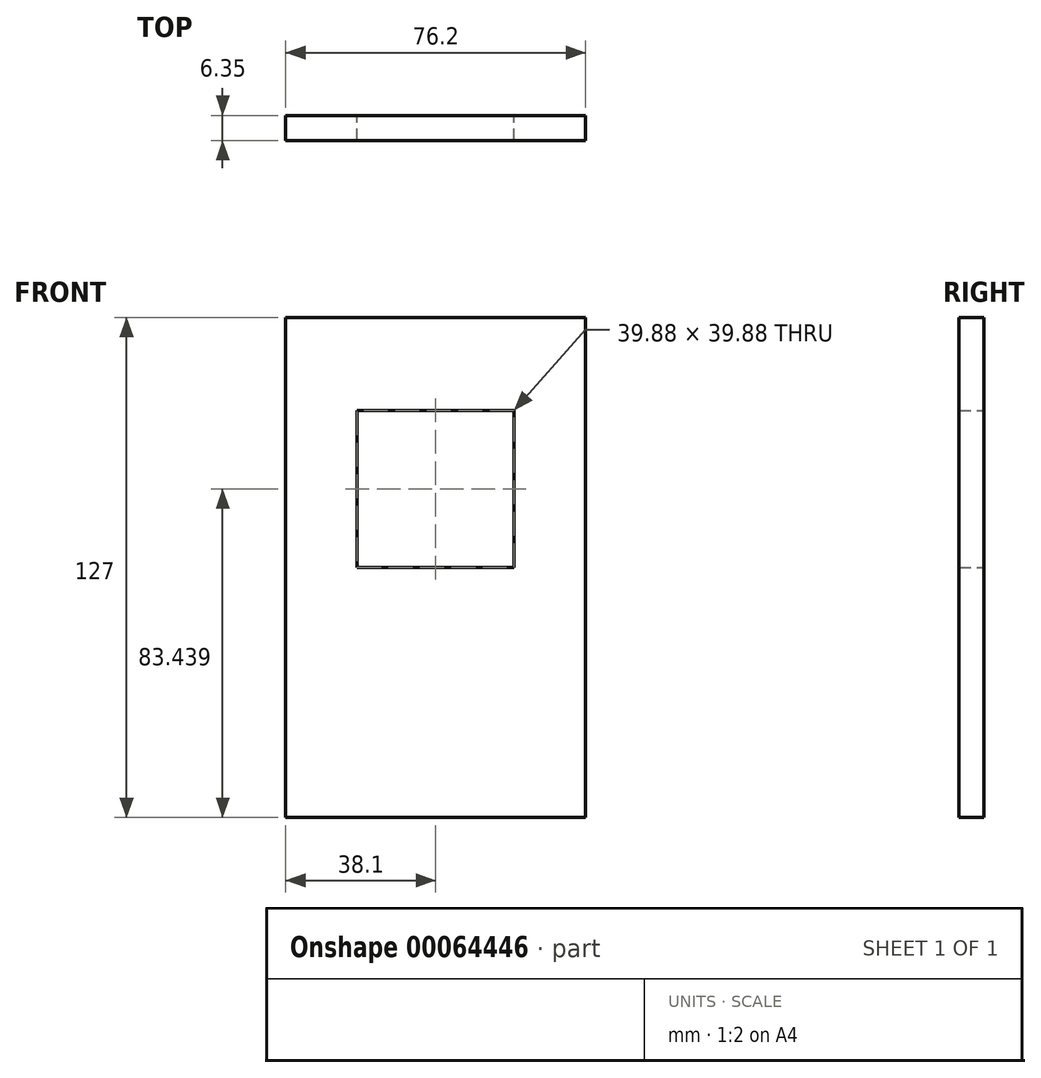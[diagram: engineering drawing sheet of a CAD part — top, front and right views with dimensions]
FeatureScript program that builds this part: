
annotation { "Feature Type Name" : "Feature", "Feature Type Description" : "" }
export const myFeature = defineFeature(function(context is Context, id is Id, definition is map)
    precondition{}
    {
        {
            var Q0;
            Q0=qCreatedBy(makeId("Front.planeOp"),FACE);
            var sketch = newSketch(context, id + "F0", { "sketchPlane" : qUnion([Q0])});
            skLineSegment(sketch, "E0.rect.bottom", {"start": v(38.1, 63.5) * mm, "end": v(-38.1, 63.5) * mm});
            skLineSegment(sketch, "E0.rect.top", {"start": v(38.1, -63.5) * mm, "end": v(-38.1, -63.5) * mm});
            skLineSegment(sketch, "E0.rect.left", {"start": v(38.1, 63.5) * mm, "end": v(38.1, -63.5) * mm});
            skLineSegment(sketch, "E0.rect.right", {"start": v(-38.1, 63.5) * mm, "end": v(-38.1, -63.5) * mm});
            skPoint(sketch, "E0.rect.middle", {"position": v(0, 0) * mm});
            skLineSegment(sketch, "E1.bottom", {"start": v(-19.94, 39.88) * mm, "end": v(19.94, 39.88) * mm});
            skLineSegment(sketch, "E1.top", {"start": v(-19.94, 0) * mm, "end": v(19.94, 0) * mm});
            skLineSegment(sketch, "E1.left", {"start": v(-19.94, 39.88) * mm, "end": v(-19.94, 0) * mm});
            skLineSegment(sketch, "E1.right", {"start": v(19.94, 39.88) * mm, "end": v(19.94, 0) * mm});
            skPoint(sketch, "E2", {"position": v(0, 63.5) * mm});
            skPoint(sketch, "E3", {"position": v(0, 39.88) * mm});
            skLineSegment(sketch, "E4", {"start": v(0, 63.5) * mm, "end": v(0, 39.88) * mm, "construction": true});
            skSolve(sketch);
        }
        {
            var Q0;
            Q0 = qSketchRegion(id + "F0", true);
            extrude(context, id + "F1", {"entities" : qUnion([Q0]), "depth" : 6.35 * mm});
        }
    });
